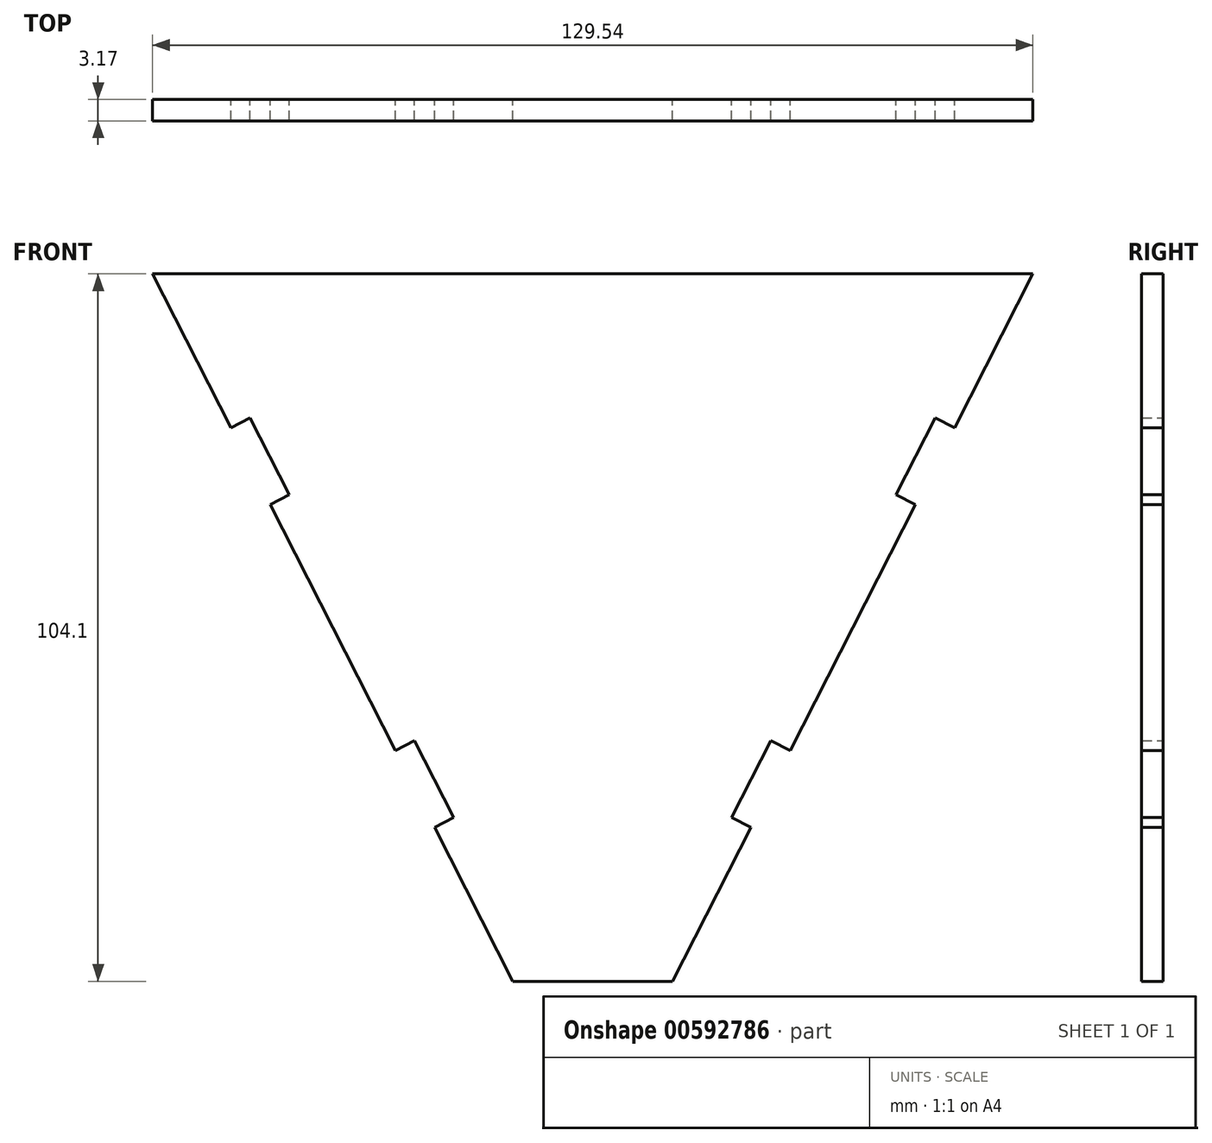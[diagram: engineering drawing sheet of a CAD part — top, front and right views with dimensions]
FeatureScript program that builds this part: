
annotation { "Feature Type Name" : "Feature", "Feature Type Description" : "" }
export const myFeature = defineFeature(function(context is Context, id is Id, definition is map)
    precondition{}
    {
        {
            var Q0;
            Q0=qCreatedBy(makeId("Front.planeOp"),FACE);
            var sketch = newSketch(context, id + "F0", { "sketchPlane" : qUnion([Q0])});
            skLineSegment(sketch, "E0.bottom", {"start": v(11.75, -52.05) * mm, "end": v(-11.75, -52.05) * mm});
            skLineSegment(sketch, "E0.top", {"start": v(64.77, 52.05) * mm, "end": v(-64.77, 52.05) * mm});
            skPoint(sketch, "E0.middle", {"position": v(0, 0) * mm});
            skLineSegment(sketch, "E1", {"start": v(0, -52.05) * mm, "end": v(-11.75, -52.05) * mm});
            skLineSegment(sketch, "E2", {"start": v(-11.75, -52.05) * mm, "end": v(0, -52.05) * mm});
            skLineSegment(sketch, "E3", {"start": v(0, -52.05) * mm, "end": v(11.75, -52.05) * mm});
            skLineSegment(sketch, "E4", {"start": v(-11.75, -52.05) * mm, "end": v(-23.28, -29.41) * mm});
            skLineSegment(sketch, "E5", {"start": v(11.75, -52.05) * mm, "end": v(23.28, -29.41) * mm});
            skPoint(sketch, "E6.orphan", {"position": v(-64.77, -52.05) * mm});
            skPoint(sketch, "E0.left.start.orphan", {"position": v(64.77, -52.05) * mm});
            skLineSegment(sketch, "E7", {"start": v(-23.28, -29.41) * mm, "end": v(-20.45, -27.97) * mm});
            skLineSegment(sketch, "E8", {"start": v(-20.45, -27.97) * mm, "end": v(-26.21, -16.65) * mm});
            skLineSegment(sketch, "E9", {"start": v(-26.21, -16.65) * mm, "end": v(-29.04, -18.1) * mm});
            skLineSegment(sketch, "E10", {"start": v(-29.04, -18.1) * mm, "end": v(-47.48, 18.1) * mm});
            skLineSegment(sketch, "E11", {"start": v(-47.48, 18.1) * mm, "end": v(-44.65, 19.54) * mm});
            skLineSegment(sketch, "E12", {"start": v(-44.65, 19.54) * mm, "end": v(-50.41, 30.85) * mm});
            skLineSegment(sketch, "E13", {"start": v(-50.41, 30.85) * mm, "end": v(-53.24, 29.41) * mm});
            skLineSegment(sketch, "E14.trimOffspring", {"start": v(-53.24, 29.41) * mm, "end": v(-64.77, 52.05) * mm});
            skLineSegment(sketch, "E15", {"start": v(23.28, -29.41) * mm, "end": v(20.45, -27.97) * mm});
            skLineSegment(sketch, "E16", {"start": v(20.45, -27.97) * mm, "end": v(26.21, -16.65) * mm});
            skLineSegment(sketch, "E17", {"start": v(26.21, -16.65) * mm, "end": v(29.04, -18.1) * mm});
            skLineSegment(sketch, "E18", {"start": v(29.04, -18.1) * mm, "end": v(47.48, 18.1) * mm});
            skLineSegment(sketch, "E19", {"start": v(47.48, 18.1) * mm, "end": v(44.65, 19.54) * mm});
            skLineSegment(sketch, "E20", {"start": v(44.65, 19.54) * mm, "end": v(50.41, 30.85) * mm});
            skLineSegment(sketch, "E21", {"start": v(50.41, 30.85) * mm, "end": v(53.24, 29.41) * mm});
            skLineSegment(sketch, "E22.trimOffspring", {"start": v(53.24, 29.41) * mm, "end": v(64.77, 52.05) * mm});
            skSolve(sketch);
        }
        {
            var Q0;
            Q0 = qSketchRegion(id + "F0", true);
            extrude(context, id + "F1", {"entities" : qUnion([Q0]), "depth" : 3.17 * mm, "offsetDistance" : 25.4 * mm});
        }
    });
